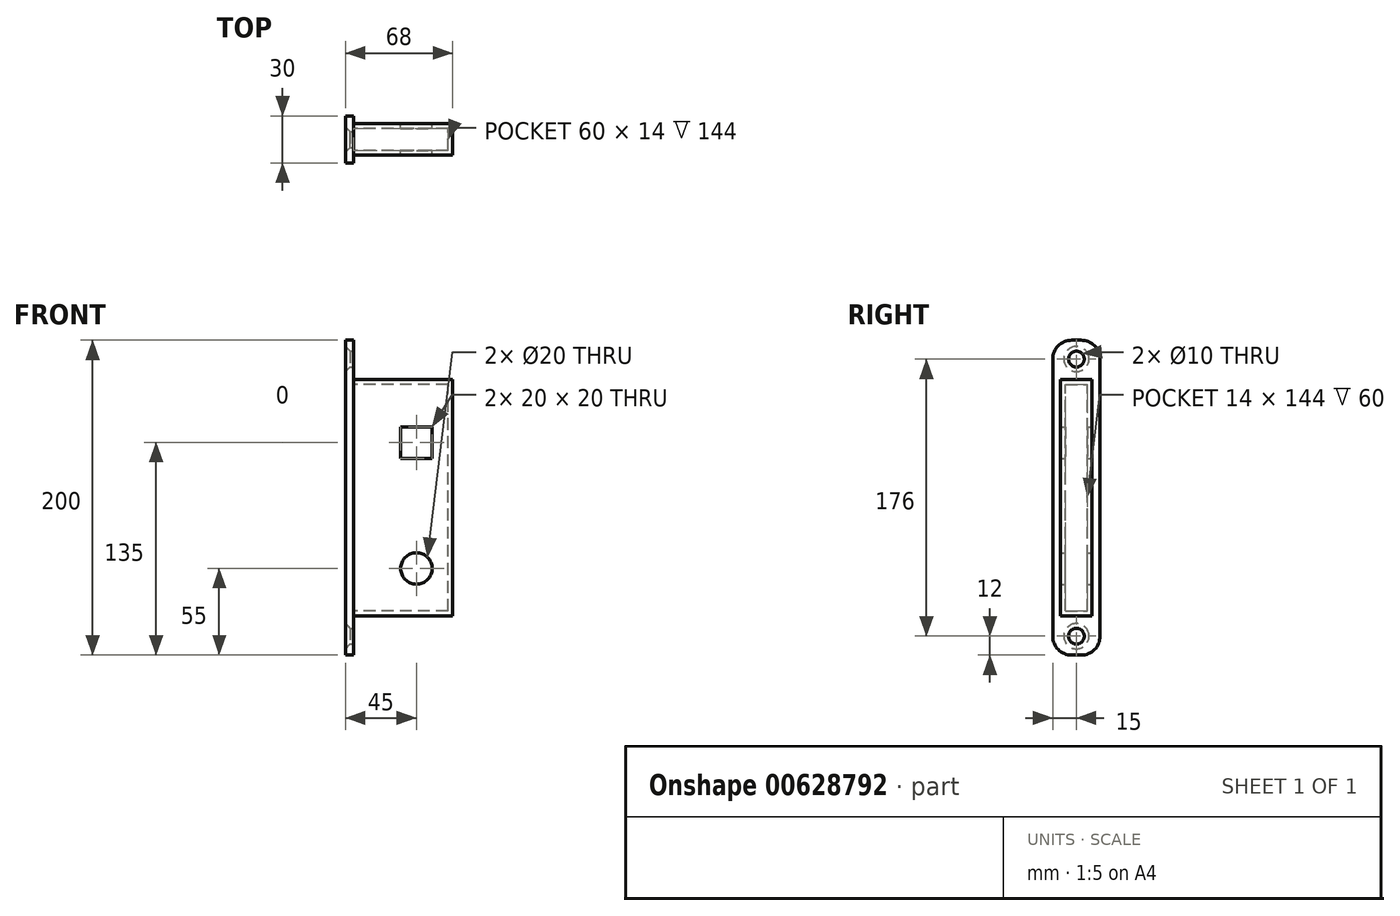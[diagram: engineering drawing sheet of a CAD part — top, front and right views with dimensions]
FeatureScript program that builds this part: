
annotation { "Feature Type Name" : "Feature", "Feature Type Description" : "" }
export const myFeature = defineFeature(function(context is Context, id is Id, definition is map)
    precondition{}
    {
        {
            var Q0;
            Q0=qCreatedBy(makeId("Front.planeOp"),FACE);
            var sketch = newSketch(context, id + "F0", { "sketchPlane" : qUnion([Q0])});
            skLineSegment(sketch, "E0.bottom", {"start": v(0, 0) * mm, "end": v(-63, 0) * mm});
            skLineSegment(sketch, "E0.top", {"start": v(0, 150) * mm, "end": v(-63, 150) * mm});
            skLineSegment(sketch, "E0.left", {"start": v(0, 0) * mm, "end": v(0, 150) * mm});
            skLineSegment(sketch, "E0.right", {"start": v(-63, 0) * mm, "end": v(-63, 150) * mm});
            skCircle(sketch, "E1", {"center": v(-23, 30) * mm, "radius": 10 * mm});
            skLineSegment(sketch, "E2.bottom", {"start": v(-13, 120) * mm, "end": v(-33, 120) * mm});
            skLineSegment(sketch, "E2.top", {"start": v(-13, 100) * mm, "end": v(-33, 100) * mm});
            skLineSegment(sketch, "E2.left", {"start": v(-13, 120) * mm, "end": v(-13, 100) * mm});
            skLineSegment(sketch, "E2.right", {"start": v(-33, 120) * mm, "end": v(-33, 100) * mm});
            skPoint(sketch, "E2.middle", {"position": v(-23, 110) * mm});
            skSolve(sketch);
        }
        {
            var Q0;
            Q0 = qSketchRegion(id + "F0", true);
            extrude(context, id + "F1", {"entities" : qUnion([Q0]), "depth" : 20 * mm, "offsetDistance" : 25 * mm});
        }
        {
            var Q0;
            Q0=makeQuery(id+"F1.opExtrude","SWEPT_FACE",FACE,{"disambiguationData":[OSD([sQuery(id+"F0.wireOp",EDGE,"E0.right")])]});
            var Q1;
            Q1=makeQuery(id+"F1.opExtrude","SWEPT_FACE",FACE,{"disambiguationData":[OSD([sQuery(id+"F0.wireOp",EDGE,"E2.left")])]});
            var Q2;
            Q2=makeQuery(id+"F1.opExtrude","SWEPT_FACE",FACE,{"disambiguationData":[OSD([sQuery(id+"F0.wireOp",EDGE,"E2.top")])]});
            var Q3;
            Q3=makeQuery(id+"F1.opExtrude","SWEPT_FACE",FACE,{"disambiguationData":[OSD([sQuery(id+"F0.wireOp",EDGE,"E2.right")])]});
            var Q4;
            Q4=makeQuery(id+"F1.opExtrude","SWEPT_FACE",FACE,{"disambiguationData":[OSD([sQuery(id+"F0.wireOp",EDGE,"E2.bottom")])]});
            var Q5;
            Q5=makeQuery(id+"F1.opExtrude","SWEPT_FACE",FACE,{"disambiguationData":[OSD([sQuery(id+"F0.wireOp",EDGE,"E1")])]});
            shell(context, id + "F2", {"entities" : qUnion([Q0, Q1, Q2, Q3, Q4, Q5]), "thickness" : 3 * mm});
        }
        {
            var Q0;
            Q0=makeQuery(id+"F1.opExtrude","SWEPT_FACE",FACE,{"disambiguationData":[OSD([sQuery(id+"F0.wireOp",EDGE,"E0.right")])]});
            var sketch = newSketch(context, id + "F3", { "sketchPlane" : qUnion([Q0])});
            skLineSegment(sketch, "E3.bottom", {"start": v(13, 175) * mm, "end": v(7, 175) * mm});
            skLineSegment(sketch, "E3.top", {"start": v(13, -25) * mm, "end": v(7, -25) * mm});
            skLineSegment(sketch, "E3.left", {"start": v(25, 163) * mm, "end": v(25, -13) * mm});
            skLineSegment(sketch, "E3.right", {"start": v(-5, 163) * mm, "end": v(-5, -13) * mm});
            skPoint(sketch, "E3.middle", {"position": v(10, 75) * mm});
            skPoint(sketch, "E3.middle.positionSnap0", {"position": v(10, 147) * mm});
            skPoint(sketch, "E3.middle.positionSnap1", {"position": v(3, 75) * mm});
            skPoint(sketch, "E3.centerSnap0", {"position": v(10, 147) * mm});
            skPoint(sketch, "E3.centerSnap1", {"position": v(3, 75) * mm});
            skCircle(sketch, "E4", {"center": v(10, 163) * mm, "radius": 5 * mm});
            skPoint(sketch, "E4.centerSnap0", {"position": v(10, 175) * mm});
            skCircle(sketch, "E5", {"center": v(10, -13) * mm, "radius": 5 * mm});
            skPoint(sketch, "E5.centerSnap0", {"position": v(10, -25) * mm});
            skPoint(sketch, "E6.visualSharp", {"position": v(-5, 175) * mm});
            skArc(sketch, "E6.filletArc", {"start": v(7, 175) * mm, "mid": v(-1.49, 171.49) * mm, "end": v(-5, 163) * mm});
            skPoint(sketch, "E7.visualSharp", {"position": v(25, 175) * mm});
            skArc(sketch, "E7.filletArc", {"start": v(25, 163) * mm, "mid": v(21.49, 171.49) * mm, "end": v(13, 175) * mm});
            skPoint(sketch, "E8.visualSharp", {"position": v(25, -25) * mm});
            skArc(sketch, "E8.filletArc", {"start": v(13, -25) * mm, "mid": v(21.49, -21.49) * mm, "end": v(25, -13) * mm});
            skPoint(sketch, "E9.visualSharp", {"position": v(-5, -25) * mm});
            skArc(sketch, "E9.filletArc", {"start": v(-5, -13) * mm, "mid": v(-1.49, -21.49) * mm, "end": v(7, -25) * mm});
            skSolve(sketch);
        }
        {
            var Q0;
            Q0 = qSketchRegion(id + "F3", true);
            extrude(context, id + "F4", {"entities" : qUnion([Q0]), "operationType" : NewBodyOperationType.ADD, "depth" : 5 * mm, "offsetDistance" : 25 * mm});
        }
        {
            var Q0;
            Q0=makeQuery(id+"F4.opExtrude","CAP_EDGE",EDGE,{"disambiguationData":[OSD([sQuery(id+"F3.wireOp",EDGE,"E4")])],"isStart":false});
            var Q1;
            Q1=makeQuery(id+"F4.opExtrude","CAP_EDGE",EDGE,{"disambiguationData":[OSD([sQuery(id+"F3.wireOp",EDGE,"E5")])],"isStart":false});
            chamfer(context, id + "F5", {"entities" : qUnion([Q0, Q1]), "width" : 3 * mm, "tangentPropagation" : true});
        }
    });
